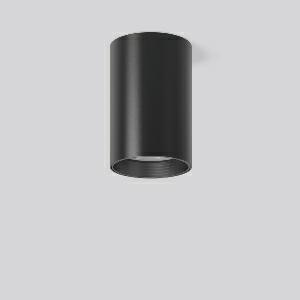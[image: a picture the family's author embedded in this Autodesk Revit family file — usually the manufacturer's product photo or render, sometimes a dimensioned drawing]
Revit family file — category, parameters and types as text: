
# Revit family: heledon_maxi_a_931234_003_adc8
name_source: partatom
category: Lighting Fixtures
units: mm (PartAtom-declared; Revit-internal decimal feet)

## family parameters
Cut with Voids When Loaded = No
Host = Face
Light Source = No
Part Type = Normal
Room Calculation Point = No
Round Connector Dimension = Use Diameter
Shared = No

## types (1)
- HELEDON maxi A (1 x LED Modul 932 fresh meat, 1800 lm, 3200)
    Apparent Load = 33 VA
    Approval mark = CE
    CIE Flux Codes = 97 100 100 100 100
    Color Rendering = 90
    Color Temperature = 3200
    Default Elevation = 1800 mm  [stored 5.90551 ft]
    Description = Series: HELEDON maxi
Cylindrical surface-mounted downlight. Housing: die-cast aluminium, powder-coated. Internal ceiling frame polycarbonate with bayonet mounting. Black plastic ring and recessed LED to prevent glare from the side. Optical assembly with lens made of plastic (polycarbonate) for the best homogeneous light distribution - can be changed without tools. Special LED for illumination of meat included. Suitable for Ceiling mounting. Easy installation with a separate ceiling frame with bayonet mounting and plug connection. Driver integrated. Connected via plug-in connector. High quality converter without flickering and stroboscopic effect. The following accessories can be mounted without use of tools: interchangeable lenses, decorative glasses, honeycomb louvre, clear and frosted diffusers, white interchangeable plastic ring. 
Colour: deep black, matt (RAL 9005)
Diameter: 123 mm
Height: 183 mm
Lamp: LED
Socket: without socket
Colour temperature: fresh meat
System power: 33 W
Rated luminous flux: 1800 lm
Luminous efficiency: 55 lm/W
Control gear: Regulated power supply
Protection class: I
Type of protection: IP 20
    Height = 183 mm
    Lamp = 1 x LED Modul 932 fresh meat
    Lamp Light Flux = 1800 lm
    Lamp count = 1
    Length = 123 mm
    Lifetime = 50000 h
    Luminous efficacy = 55 lm/W
    Manufacturer = RZB
    ModVariant = No
    Model = 931234.003
    Mounting Place = Ceiling
    Mounting Type = Surface mounted
    Number of Poles = 1
    OnlyDefault = Yes
    Power Factor = 1
    Product Name = HELEDON maxi A
    Product group = Surface mounted downlights
    ProductGroupID = 302
    Protection Class = Protection class I
    Protection Degree = IP 20
    RLX_Detail_Level = 1
    RLX_Emergency_Light_Flux = 0 lm
    RLX_Emergency_Type = 0
    RLX_Emergency_Type_DB = No
    RlxData = <blob elided: 98825 chars, md5=6f6bcb3f>
    Socket = socket
    Standby Power = 0 W
    System Light Flux = 1800 lm
    System Power = 33 W
    Type Comments = Product without accessories
    Type Image = 931193.003.jpg
    URL = http://relux.com
    VarID = ---
    Voltage = 230 V
    Voltage Range = 220-240 V
    Weight = 0.00 kg
    Width = 0 mm  [stored 0 ft]

note: [stored X ft] marks values corroborated as IEEE doubles in the binary element streams (Revit-internal decimal feet)

## geometry (parser evidence)
native form markers: Blend x4, Sweep x9
no freeform markers — native parametric forms only
